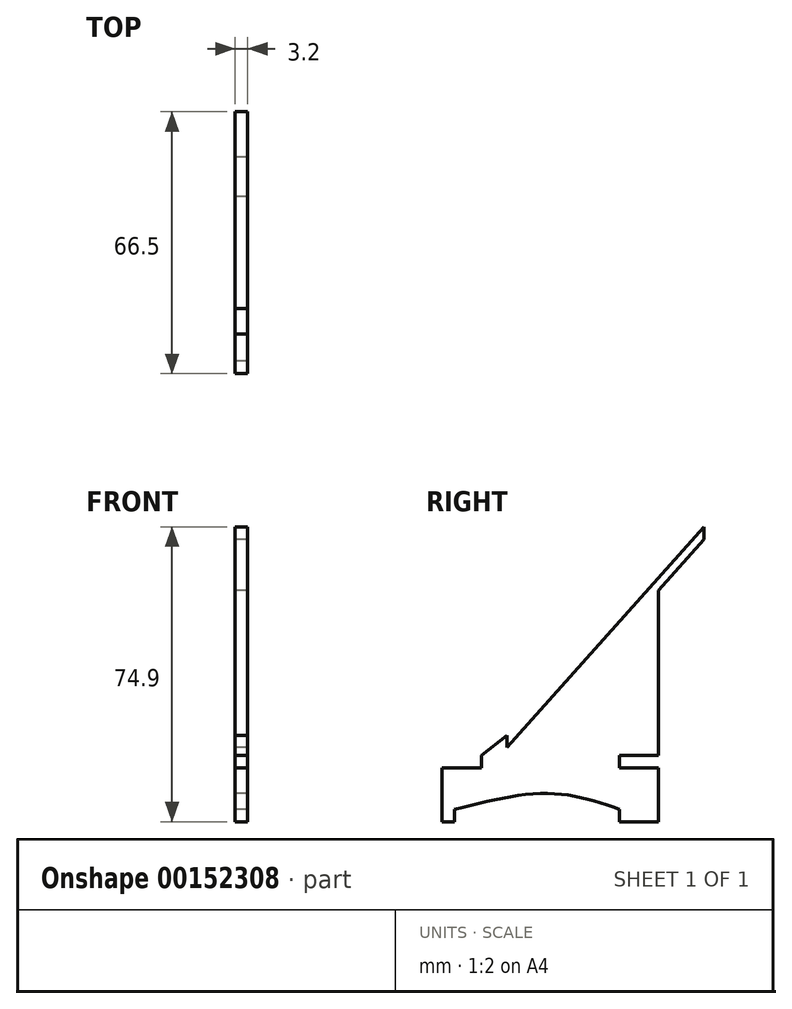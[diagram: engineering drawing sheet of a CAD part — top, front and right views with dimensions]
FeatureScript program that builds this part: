
annotation { "Feature Type Name" : "Feature", "Feature Type Description" : "" }
export const myFeature = defineFeature(function(context is Context, id is Id, definition is map)
    precondition{}
    {
        {
            var Q0;
            Q0=qCreatedBy(makeId("Right.planeOp"),FACE);
            var sketch = newSketch(context, id + "F0", { "sketchPlane" : qUnion([Q0])});
            skLineSegment(sketch, "E0", {"start": v(0, 0) * mm, "end": v(-24.3, 0) * mm, "construction": true});
            skLineSegment(sketch, "E1", {"start": v(-24.3, 0) * mm, "end": v(0, 0) * mm, "construction": true});
            skLineSegment(sketch, "E2.top", {"start": v(-27.5, -3.2) * mm, "end": v(-24.3, -3.2) * mm});
            skLineSegment(sketch, "E2.left", {"start": v(-27.5, 0) * mm, "end": v(-27.5, -3.2) * mm});
            skLineSegment(sketch, "E2.right", {"start": v(-24.3, 0) * mm, "end": v(-24.3, -3.2) * mm});
            skLineSegment(sketch, "E3.left", {"start": v(27.5, 0) * mm, "end": v(27.5, -3.2) * mm});
            skLineSegment(sketch, "E4", {"start": v(0, 0) * mm, "end": v(0, 4) * mm, "construction": true});
            skLineSegment(sketch, "E5", {"start": v(-27.5, 0) * mm, "end": v(-27.5, 10.5) * mm});
            skLineSegment(sketch, "E6", {"start": v(-27.5, 10.5) * mm, "end": v(-17.5, 10.5) * mm});
            skLineSegment(sketch, "E7", {"start": v(27.5, 10.5) * mm, "end": v(27.5, 0) * mm});
            skLineSegment(sketch, "E8", {"start": v(-24.3, 0) * mm, "end": v(-7.63, 0) * mm, "construction": true});
            skLineSegment(sketch, "E9", {"start": v(-27.5, 10.5) * mm, "end": v(-11, 10.5) * mm, "construction": true});
            skLineSegment(sketch, "E10", {"start": v(-27.5, 10.5) * mm, "end": v(-17.5, 10.5) * mm, "construction": true});
            skLineSegment(sketch, "E11", {"start": v(-17.5, 10.5) * mm, "end": v(-17.5, 13.7) * mm});
            skLineSegment(sketch, "E12", {"start": v(17.5, 13.7) * mm, "end": v(17.5, 10.5) * mm});
            skLineSegment(sketch, "E13.trimOffspring", {"start": v(17.5, 10.5) * mm, "end": v(27.5, 10.5) * mm});
            skLineSegment(sketch, "E14", {"start": v(-11, 10.5) * mm, "end": v(-11, 13.7) * mm, "construction": true});
            skLineSegment(sketch, "E15", {"start": v(-11, 13.7) * mm, "end": v(-11, 18.7) * mm, "construction": true});
            skLineSegment(sketch, "E16", {"start": v(-11, 18.7) * mm, "end": v(-11, 15.7) * mm});
            skLineSegment(sketch, "E17", {"start": v(-11, 15.7) * mm, "end": v(39, 15.7) * mm, "construction": true});
            skLineSegment(sketch, "E18", {"start": v(39, 15.7) * mm, "end": v(39, 71.7) * mm, "construction": true});
            skLineSegment(sketch, "E19", {"start": v(39, 71.7) * mm, "end": v(-11, 15.7) * mm});
            skLineSegment(sketch, "E20", {"start": v(-27.5, 10.5) * mm, "end": v(-27.5, 13.7) * mm, "construction": true});
            skLineSegment(sketch, "E21", {"start": v(-27.5, 13.7) * mm, "end": v(-17.5, 13.7) * mm, "construction": true});
            skLineSegment(sketch, "E22", {"start": v(17.5, 13.7) * mm, "end": v(27.5, 13.7) * mm, "construction": true});
            skLineSegment(sketch, "E23", {"start": v(27.5, 13.7) * mm, "end": v(27.5, 10.5) * mm, "construction": true});
            skLineSegment(sketch, "E24", {"start": v(-11, 15.7) * mm, "end": v(-8.14, 15.7) * mm, "construction": true});
            skLineSegment(sketch, "E25", {"start": v(-8.14, 15.7) * mm, "end": v(39, 68.5) * mm, "construction": true});
            skLineSegment(sketch, "E26", {"start": v(27.5, 13.7) * mm, "end": v(27.5, 55.62) * mm});
            skLineSegment(sketch, "E27", {"start": v(27.5, 55.62) * mm, "end": v(39, 68.5) * mm});
            skLineSegment(sketch, "E28", {"start": v(39, 71.7) * mm, "end": v(39, 68.5) * mm});
            skLineSegment(sketch, "E29", {"start": v(27.5, 13.7) * mm, "end": v(17.5, 13.7) * mm});
            skLineSegment(sketch, "E30", {"start": v(27.5, -3.2) * mm, "end": v(17.5, -3.2) * mm});
            skLineSegment(sketch, "E31", {"start": v(17.5, -3.2) * mm, "end": v(17.5, 0) * mm});
            skFitSpline(sketch, "E32", {"points": [v(-24.3, 0) * mm, v(0, 4) * mm, v(17.5, 0) * mm], "startDerivative": vector(46.95, 11.76) * mm, "endDerivative": vector(36.37, -12.4) * mm});
            skLineSegment(sketch, "E33", {"start": v(-17.5, 13.7) * mm, "end": v(-11, 18.7) * mm});
            skSolve(sketch);
        }
        {
            var Q0;
            Q0=makeQuery(id+"F0.imprint","IMPRINT",FACE,{"disambiguationData":[TD([[makeQuery(id+"F0.imprint","IMPRINT",EDGE,{"derivedFrom":sQuery(id+"F0.wireOp",EDGE,"E2.bottom")}),1.0]])]});
            var Q1;
            Q1=makeQuery(id+"F0.imprint","IMPRINT",FACE,{"disambiguationData":[TD([[makeQuery(id+"F0.imprint","IMPRINT",EDGE,{"derivedFrom":sQuery(id+"F0.wireOp",EDGE,"E2.top")}),1.0]])]});
            extrude(context, id + "F1", {"entities" : qUnion([Q0, Q1]), "endBound" : BoundingType.SYMMETRIC, "depth" : 3.2 * mm});
        }
    });
